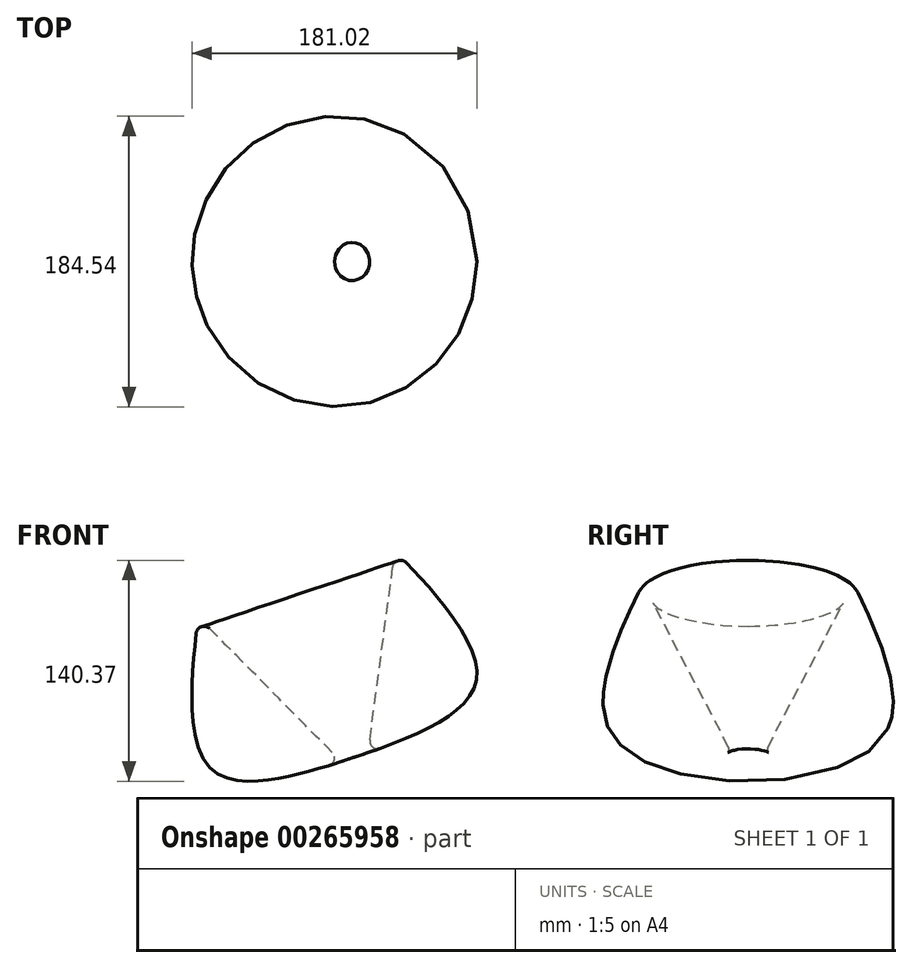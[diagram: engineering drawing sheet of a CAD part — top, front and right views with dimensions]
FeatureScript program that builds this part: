
annotation { "Feature Type Name" : "Feature", "Feature Type Description" : "" }
export const myFeature = defineFeature(function(context is Context, id is Id, definition is map)
    precondition{}
    {
        {
            var Q0;
            Q0=qCreatedBy(makeId("Front.planeOp"),FACE);
            var sketch = newSketch(context, id + "F0", { "sketchPlane" : qUnion([Q0])});
            skFitSpline(sketch, "E0", {"points": [v(-17.13, -55.4) * mm, v(51.69, 0) * mm, v(0, 73.4) * mm, v(0, 73.68) * mm], "startDerivative": vector(226.35, 85.52) * mm, "endDerivative": vector(5.1, 5.86) * mm});
            skLineSegment(sketch, "E1", {"start": v(0, 73.68) * mm, "end": v(-17.13, -55.4) * mm});
            skLineSegment(sketch, "E2", {"start": v(-66.54, 63.97) * mm, "end": v(-23.13, -65.4) * mm});
            skSolve(sketch);
        }
        {
            var Q0;
            {var subQ0=sQuery(id+"F0.wireOp",EDGE,"E1");var subQ1=sQuery(id+"F0.wireOp",EDGE,"E0");var subQ2=makeQuery(id+"F0.imprint","INTERSECT",VERTEX,{"disambiguationData":[OD(0.0)],"derivedFrom":[subQ1,subQ0]});Q0=makeQuery(id+"F0.imprint","IMPRINT",FACE,{"disambiguationData":[TD([[makeQuery(id+"F0.imprint","IMPRINT",EDGE,{"disambiguationData":[TD([[subQ2,-1.0]])],"derivedFrom":subQ1}),1.0]])]});}
            var Q1;
            Q1=sQuery(id+"F0.wireOp",EDGE,"E2");
            revolve(context, id + "F1", {"entities" : qUnion([Q0]), "axis" : qUnion([Q1]), "revolveType" : RevolveType.FULL});
        }
        {
            var Q0;
            Q0=makeQuery(id+"F1.opRevolve","SWEPT_FACE",FACE,{"disambiguationData":[OSD([sQuery(id+"F0.wireOp",EDGE,"E1")])]});
            fillet(context, id + "F2", {"entities" : qUnion([Q0]), "radius" : 5.08 * mm, "tangentPropagation" : true, "allowEdgeOverflow" : false});
        }
    });
